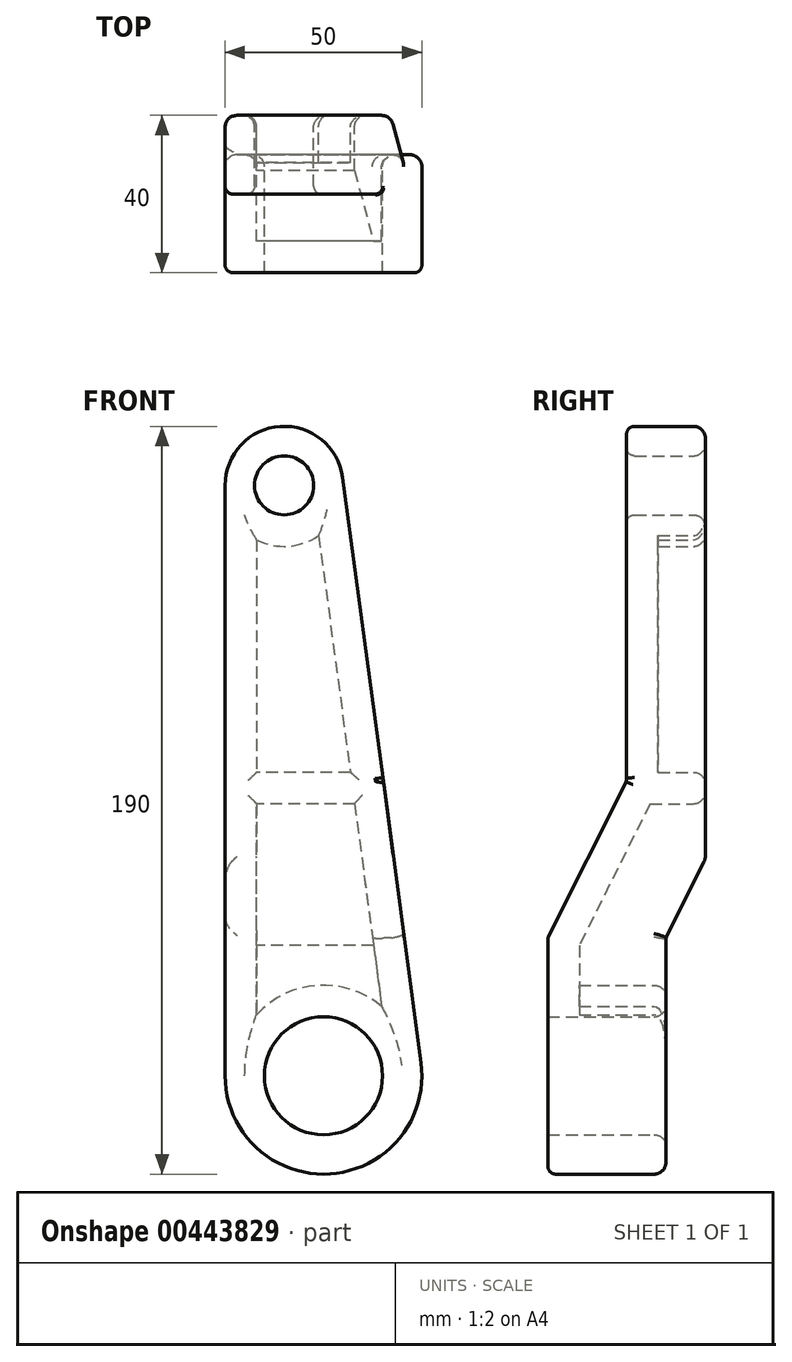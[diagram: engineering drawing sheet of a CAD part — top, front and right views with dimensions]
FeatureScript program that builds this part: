
annotation { "Feature Type Name" : "Feature", "Feature Type Description" : "" }
export const myFeature = defineFeature(function(context is Context, id is Id, definition is map)
    precondition{}
    {
        {
            var Q0;
            Q0=qCreatedBy(makeId("Front.planeOp"),FACE);
            var sketch = newSketch(context, id + "F0", { "sketchPlane" : qUnion([Q0])});
            skCircle(sketch, "E0", {"center": v(0, 0) * mm, "radius": 25 * mm});
            skCircle(sketch, "E1", {"center": v(-10, 150) * mm, "radius": 15 * mm});
            skLineSegment(sketch, "E2", {"start": v(-25, 150) * mm, "end": v(-25, 0) * mm});
            skLineSegment(sketch, "E3", {"start": v(4.87, 152) * mm, "end": v(24.78, 3.32) * mm});
            skSolve(sketch);
        }
        {
            var Q0;
            Q0 = qSketchRegion(id + "F0", true);
            extrude(context, id + "F1", {"entities" : qUnion([Q0]), "depth" : 40 * mm});
        }
        {
            var Q0;
            Q0=makeQuery(id+"F1.opExtrude","SWEPT_FACE",FACE,{"disambiguationData":[OSD([sQuery(id+"F0.wireOp",EDGE,"E2")])]});
            var sketch = newSketch(context, id + "F2", { "sketchPlane" : qUnion([Q0])});
            skLineSegment(sketch, "E4", {"start": v(10, -40.07) * mm, "end": v(10, 35) * mm});
            skLineSegment(sketch, "E5", {"start": v(10, 35) * mm, "end": v(0, 55) * mm});
            skLineSegment(sketch, "E6", {"start": v(0, 55) * mm, "end": v(0, -40.07) * mm});
            skLineSegment(sketch, "E7", {"start": v(40, 166.97) * mm, "end": v(40, 35) * mm});
            skLineSegment(sketch, "E8", {"start": v(40, 35) * mm, "end": v(20, 75) * mm});
            skLineSegment(sketch, "E9", {"start": v(20, 75) * mm, "end": v(20, 166.97) * mm});
            skLineSegment(sketch, "E10", {"start": v(0, -40.07) * mm, "end": v(10, -40.07) * mm});
            skLineSegment(sketch, "E11", {"start": v(20, 166.97) * mm, "end": v(40, 166.97) * mm});
            skSolve(sketch);
        }
        {
            var Q0;
            Q0 = qSketchRegion(id + "F2", true);
            extrude(context, id + "F3", {"entities" : qUnion([Q0]), "operationType" : NewBodyOperationType.REMOVE, "endBound" : BoundingType.THROUGH_ALL, "oppositeDirection" : true, "depth" : 25 * mm});
        }
        {
            var Q0;
            Q0=makeQuery(id+"F1.opExtrude","CAP_FACE",FACE,{"disambiguationData":[OSD([sQuery(id+"F0.wireOp",EDGE,"E0"),sQuery(id+"F0.wireOp",EDGE,"E1"),sQuery(id+"F0.wireOp",EDGE,"E2"),sQuery(id+"F0.wireOp",EDGE,"E3")])],"isStart":true});
            var sketch = newSketch(context, id + "F4", { "sketchPlane" : qUnion([Q0])});
            skCircle(sketch, "E12", {"center": v(10, 150) * mm, "radius": 7.5 * mm});
            skCircle(sketch, "E13", {"center": v(0, 0) * mm, "radius": 15 * mm});
            skSolve(sketch);
        }
        {
            var Q0;
            Q0 = qSketchRegion(id + "F4", true);
            extrude(context, id + "F5", {"entities" : qUnion([Q0]), "operationType" : NewBodyOperationType.REMOVE, "endBound" : BoundingType.THROUGH_ALL, "oppositeDirection" : true, "depth" : 25 * mm});
        }
        {
            var Q0;
            Q0=makeQuery(id+"F1.opExtrude","CAP_FACE",FACE,{"disambiguationData":[OSD([sQuery(id+"F0.wireOp",EDGE,"E0"),sQuery(id+"F0.wireOp",EDGE,"E1"),sQuery(id+"F0.wireOp",EDGE,"E2"),sQuery(id+"F0.wireOp",EDGE,"E3")])],"isStart":true});
            var Q1;
            Q1=makeQuery(id+"F3.boolean.opBoolean","COPY",FACE,{"derivedFrom":makeQuery(id+"F3.opExtrude","SWEPT_FACE",FACE,{"disambiguationData":[OSD([sQuery(id+"F2.wireOp",EDGE,"E5")])]})});
            var Q2;
            Q2=makeQuery(id+"F3.boolean.opBoolean","COPY",FACE,{"derivedFrom":makeQuery(id+"F3.opExtrude","SWEPT_FACE",FACE,{"disambiguationData":[OSD([sQuery(id+"F2.wireOp",EDGE,"E4")])]})});
            shell(context, id + "F6", {"entities" : qUnion([Q0, Q1, Q2]), "thickness" : 8 * mm});
        }
        {
            var Q0;
            Q0=makeQuery(id+"F1.opExtrude","CAP_FACE",FACE,{"disambiguationData":[OSD([sQuery(id+"F0.wireOp",EDGE,"E0"),sQuery(id+"F0.wireOp",EDGE,"E1"),sQuery(id+"F0.wireOp",EDGE,"E2"),sQuery(id+"F0.wireOp",EDGE,"E3")])],"isStart":true});
            var sketch = newSketch(context, id + "F7", { "sketchPlane" : qUnion([Q0])});
            skLineSegment(sketch, "E14", {"start": v(-6.82, 77.11) * mm, "end": v(17, 77.11) * mm});
            skLineSegment(sketch, "E15", {"start": v(-7.9, 69.11) * mm, "end": v(17, 69.11) * mm});
            skLineSegment(sketch, "E16.0", {"start": v(1.23, 137.22) * mm, "end": v(-9.79, 55) * mm});
            skLineSegment(sketch, "E17.0", {"start": v(17, 136.17) * mm, "end": v(17, 55) * mm});
            skSolve(sketch);
        }
        {
            var Q0;
            {var subQ0=sQuery(id+"F7.wireOp",EDGE,"E14");Q0=makeQuery(id+"F7.imprint","IMPRINT",FACE,{"disambiguationData":[TD([[makeQuery(id+"F7.imprint","IMPRINT",EDGE,{"derivedFrom":subQ0}),-1.0]])]});}
            extrude(context, id + "F8", {"entities" : qUnion([Q0]), "operationType" : NewBodyOperationType.ADD, "endBound" : BoundingType.UP_TO_NEXT, "oppositeDirection" : true, "depth" : 25 * mm});
        }
        {
            var Q0;
            Q0=makeQuery(id+"F1.opExtrude","CAP_EDGE",EDGE,{"disambiguationData":[OSD([sQuery(id+"F0.wireOp",EDGE,"E2")])],"isStart":true});
            var Q1;
            Q1=makeQuery(id+"F1.opExtrude","CAP_EDGE",EDGE,{"disambiguationData":[OSD([sQuery(id+"F0.wireOp",EDGE,"E1")])],"isStart":true});
            var Q2;
            Q2=makeQuery(id+"F1.opExtrude","CAP_EDGE",EDGE,{"disambiguationData":[OSD([sQuery(id+"F0.wireOp",EDGE,"E3")])],"isStart":true});
            var Q3;
            Q3=makeQuery(id+"F3.boolean.opBoolean","COPY",EDGE,{"derivedFrom":makeQuery(id+"F3.opExtrude","CAP_EDGE",EDGE,{"disambiguationData":[OSD([sQuery(id+"F2.wireOp",EDGE,"E5")])],"isStart":true})});
            var Q4;
            Q4=makeQuery(id+"F3.boolean.opBoolean","COPY",EDGE,{"derivedFrom":makeQuery(id+"F3.opExtrude","CAP_EDGE",EDGE,{"disambiguationData":[OSD([sQuery(id+"F2.wireOp",EDGE,"E4")])],"isStart":true})});
            var Q5;
            Q5=makeQuery(id+"F3.boolean.opBoolean","INTERSECT",EDGE,{"derivedFrom":[makeQuery(id+"F1.opExtrude","SWEPT_FACE",FACE,{"disambiguationData":[OSD([sQuery(id+"F0.wireOp",EDGE,"E3")])]}),makeQuery(id+"F3.opExtrude","SWEPT_FACE",FACE,{"disambiguationData":[OSD([sQuery(id+"F2.wireOp",EDGE,"E5")])]})]});
            var Q6;
            Q6=makeQuery(id+"F3.boolean.opBoolean","INTERSECT",EDGE,{"derivedFrom":[makeQuery(id+"F1.opExtrude","SWEPT_FACE",FACE,{"disambiguationData":[OSD([sQuery(id+"F0.wireOp",EDGE,"E3")])]}),makeQuery(id+"F3.opExtrude","SWEPT_FACE",FACE,{"disambiguationData":[OSD([sQuery(id+"F2.wireOp",EDGE,"E4")])]})]});
            var Q7;
            Q7=makeQuery(id+"F3.boolean.opBoolean","INTERSECT",EDGE,{"derivedFrom":[makeQuery(id+"F1.opExtrude","SWEPT_FACE",FACE,{"disambiguationData":[OSD([sQuery(id+"F0.wireOp",EDGE,"E0")])]}),makeQuery(id+"F3.opExtrude","SWEPT_FACE",FACE,{"disambiguationData":[OSD([sQuery(id+"F2.wireOp",EDGE,"E4")])]})]});
            var Q8;
            Q8=makeQuery(id+"F5.boolean.opBoolean","INTERSECT",EDGE,{"derivedFrom":[makeQuery(id+"F3.boolean.opBoolean","COPY",FACE,{"derivedFrom":makeQuery(id+"F3.opExtrude","SWEPT_FACE",FACE,{"disambiguationData":[OSD([sQuery(id+"F2.wireOp",EDGE,"E4")])]})}),makeQuery(id+"F5.opExtrude","SWEPT_FACE",FACE,{"disambiguationData":[OSD([sQuery(id+"F4.wireOp",EDGE,"E13")])]})]});
            var Q9;
            Q9=makeQuery(id+"F6.opShell","OFFSET_EDGE",EDGE,{"disambiguationData":[OSD([sQuery(id+"F2.wireOp",EDGE,"E4"),sQuery(id+"F4.wireOp",EDGE,"E13")])]});
            var Q10;
            Q10=makeQuery(id+"F6.opShell","OFFSET_EDGE",EDGE,{"disambiguationData":[OSD([sQuery(id+"F0.wireOp",EDGE,"E3"),sQuery(id+"F2.wireOp",EDGE,"E5")])]});
            var Q11;
            Q11=makeQuery(id+"F6.opShell","OFFSET_EDGE",EDGE,{"disambiguationData":[OSD([sQuery(id+"F0.wireOp",EDGE,"E3"),sQuery(id+"F2.wireOp",EDGE,"E4")])]});
            var Q12;
            Q12=makeQuery(id+"F6.opShell","OFFSET_EDGE",EDGE,{"disambiguationData":[OSD([sQuery(id+"F2.wireOp",EDGE,"E4")])]});
            var Q13;
            {var subQ0=sQuery(id+"F0.wireOp",EDGE,"E2");Q13=makeQuery(id+"F8.boolean.opBoolean","SPLIT",EDGE,{"disambiguationData":[TD([makeQuery(id+"F3.boolean.opBoolean","COPY",FACE,{"derivedFrom":makeQuery(id+"F3.opExtrude","SWEPT_FACE",FACE,{"disambiguationData":[OSD([sQuery(id+"F2.wireOp",EDGE,"E5")])]})})])],"derivedFrom":makeQuery(id+"F6.opShell","OFFSET_EDGE",EDGE,{"disambiguationData":[OSD([subQ0]),TDD([makeQuery(id+"F1.opExtrude","CAP_EDGE",EDGE,{"disambiguationData":[OSD([subQ0])],"isStart":true})])]})});}
            var Q14;
            Q14=makeQuery(id+"F8.opExtrude","CAP_EDGE",EDGE,{"disambiguationData":[OSD([sQuery(id+"F7.wireOp",EDGE,"E15")])],"isStart":true});
            var Q15;
            Q15=makeQuery(id+"F6.opShell","OFFSET_EDGE",EDGE,{"disambiguationData":[OSD([sQuery(id+"F2.wireOp",EDGE,"E5")])]});
            var Q16;
            {var subQ0=sQuery(id+"F0.wireOp",EDGE,"E3");Q16=makeQuery(id+"F8.boolean.opBoolean","SPLIT",EDGE,{"disambiguationData":[TD([makeQuery(id+"F6.opShell","OFFSET_FACE",FACE,{"disambiguationData":[OSD([sQuery(id+"F2.wireOp",EDGE,"E5")])]})])],"derivedFrom":makeQuery(id+"F6.opShell","OFFSET_EDGE",EDGE,{"disambiguationData":[OSD([subQ0]),TDD([makeQuery(id+"F1.opExtrude","CAP_EDGE",EDGE,{"disambiguationData":[OSD([subQ0])],"isStart":true})])]})});}
            var Q17;
            {var subQ1=sQuery(id+"F0.wireOp",EDGE,"E3");Q17=makeQuery(id+"F8.boolean.opBoolean","SPLIT",EDGE,{"disambiguationData":[TD([makeQuery(id+"F6.opShell","OFFSET_FACE",FACE,{"disambiguationData":[OSD([sQuery(id+"F4.wireOp",EDGE,"E12")])]})])],"derivedFrom":makeQuery(id+"F6.opShell","OFFSET_EDGE",EDGE,{"disambiguationData":[OSD([subQ1]),TDD([makeQuery(id+"F1.opExtrude","CAP_EDGE",EDGE,{"disambiguationData":[OSD([subQ1])],"isStart":true})])]})});}
            var Q18;
            Q18=makeQuery(id+"F8.boolean.opBoolean","MERGE",FACE,{"derivedFrom":[makeQuery(id+"F1.opExtrude","CAP_FACE",FACE,{"disambiguationData":[OSD([sQuery(id+"F0.wireOp",EDGE,"E0"),sQuery(id+"F0.wireOp",EDGE,"E1"),sQuery(id+"F0.wireOp",EDGE,"E2"),sQuery(id+"F0.wireOp",EDGE,"E3")])],"isStart":true}),makeQuery(id+"F8.opExtrude","CAP_FACE",FACE,{"disambiguationData":[OSD([sQuery(id+"F7.wireOp",EDGE,"E14"),sQuery(id+"F7.wireOp",EDGE,"E15"),sQuery(id+"F7.wireOp",EDGE,"E16.0"),sQuery(id+"F7.wireOp",EDGE,"E17.0")])],"isStart":true})]});
            fillet(context, id + "F9", {"entities" : qUnion([Q0, Q1, Q2, Q3, Q4, Q5, Q6, Q7, Q8, Q9, Q10, Q11, Q12, Q13, Q14, Q15, Q16, Q17, Q18]), "radius" : 3 * mm, "tangentPropagation" : true, "allowEdgeOverflow" : false});
        }
        {
            var Q0;
            Q0=makeQuery(id+"F3.boolean.opBoolean","COPY",FACE,{"derivedFrom":makeQuery(id+"F3.opExtrude","SWEPT_FACE",FACE,{"disambiguationData":[OSD([sQuery(id+"F2.wireOp",EDGE,"E8")])]})});
            var Q1;
            Q1=makeQuery(id+"F3.boolean.opBoolean","COPY",FACE,{"derivedFrom":makeQuery(id+"F3.opExtrude","SWEPT_FACE",FACE,{"disambiguationData":[OSD([sQuery(id+"F2.wireOp",EDGE,"E9")])]})});
            var Q2;
            Q2=makeQuery(id+"F1.opExtrude","CAP_EDGE",EDGE,{"disambiguationData":[OSD([sQuery(id+"F0.wireOp",EDGE,"E0")])],"isStart":false});
            var Q3;
            Q3=makeQuery(id+"F1.opExtrude","CAP_EDGE",EDGE,{"disambiguationData":[OSD([sQuery(id+"F0.wireOp",EDGE,"E3")])],"isStart":false});
            var Q4;
            Q4=makeQuery(id+"F1.opExtrude","CAP_EDGE",EDGE,{"disambiguationData":[OSD([sQuery(id+"F0.wireOp",EDGE,"E2")])],"isStart":false});
            fillet(context, id + "F10", {"entities" : qUnion([Q0, Q1, Q2, Q3, Q4]), "radius" : 2 * mm, "tangentPropagation" : true, "allowEdgeOverflow" : false});
        }
    });
